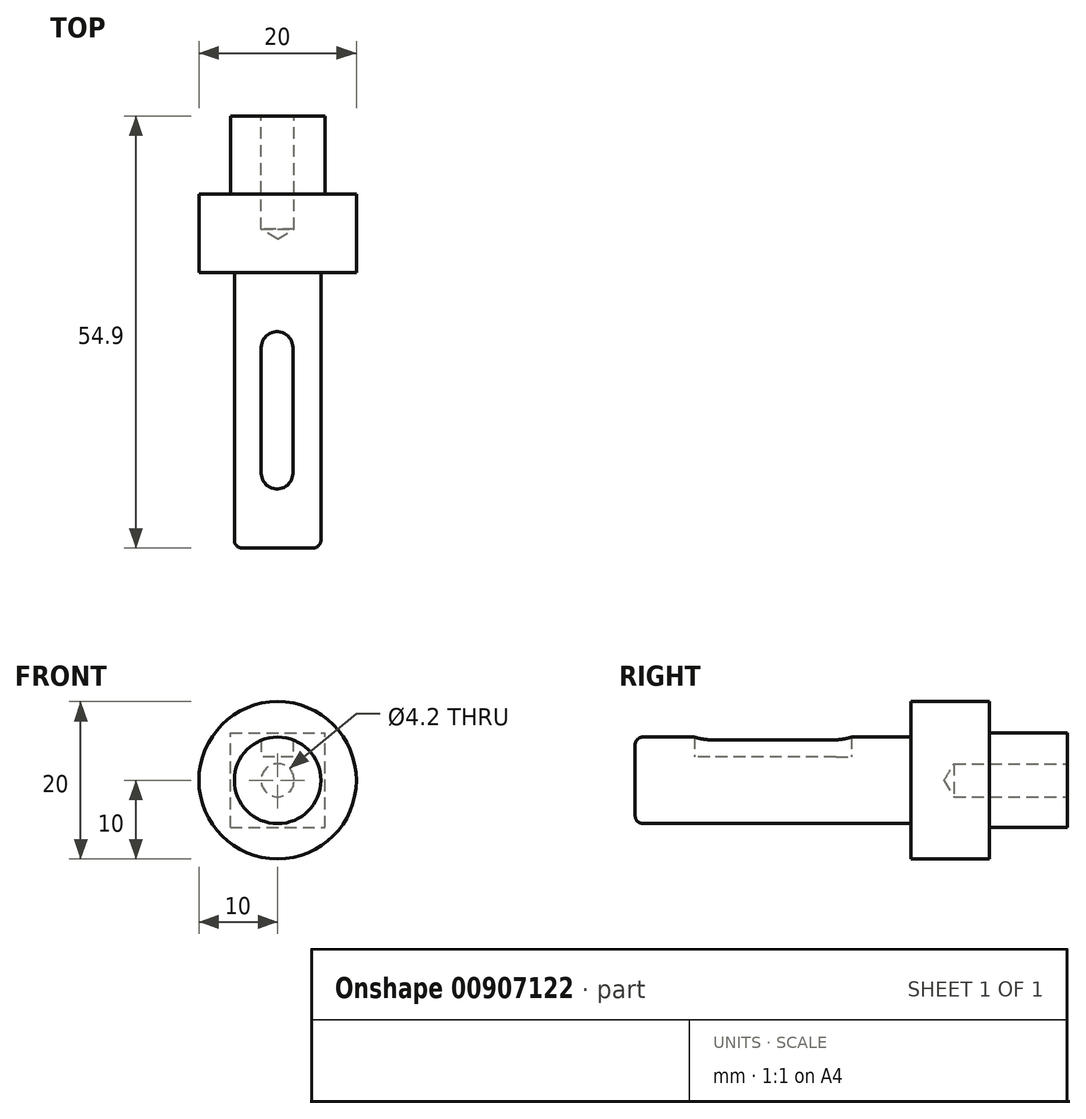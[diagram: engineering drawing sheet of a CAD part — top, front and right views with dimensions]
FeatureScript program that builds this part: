
annotation { "Feature Type Name" : "Feature", "Feature Type Description" : "" }
export const myFeature = defineFeature(function(context is Context, id is Id, definition is map)
    precondition{}
    {
        {
            var Q0;
            Q0=qCreatedBy(makeId("Front.planeOp"),FACE);
            var sketch = newSketch(context, id + "F0", { "sketchPlane" : qUnion([Q0])});
            skCircle(sketch, "E0", {"center": v(0, 0) * mm, "radius": 5.5 * mm});
            skSolve(sketch);
        }
        {
            var Q0;
            Q0 = qSketchRegion(id + "F0", true);
            extrude(context, id + "F1", {"entities" : qUnion([Q0]), "depth" : 35 * mm, "offsetDistance" : 25 * mm});
        }
        {
            var Q0;
            Q0=qCreatedBy(makeId("Front.planeOp"),FACE);
            var sketch = newSketch(context, id + "F2", { "sketchPlane" : qUnion([Q0])});
            skCircle(sketch, "E1", {"center": v(0, 0) * mm, "radius": 10 * mm});
            skSolve(sketch);
        }
        {
            var Q0;
            Q0 = qSketchRegion(id + "F2", true);
            extrude(context, id + "F3", {"entities" : qUnion([Q0]), "operationType" : NewBodyOperationType.ADD, "oppositeDirection" : true, "depth" : 10 * mm, "offsetDistance" : 25 * mm});
        }
        {
            var Q0;
            Q0=makeQuery(id+"F3.opExtrude","CAP_FACE",FACE,{"disambiguationData":[OSD([sQuery(id+"F2.wireOp",EDGE,"E1")])],"isStart":false});
            var sketch = newSketch(context, id + "F4", { "sketchPlane" : qUnion([Q0])});
            skLineSegment(sketch, "E2.bottom", {"start": v(6, -6) * mm, "end": v(-6, -6) * mm});
            skLineSegment(sketch, "E2.top", {"start": v(6, 6) * mm, "end": v(-6, 6) * mm});
            skLineSegment(sketch, "E2.left", {"start": v(6, -6) * mm, "end": v(6, 6) * mm});
            skLineSegment(sketch, "E2.right", {"start": v(-6, -6) * mm, "end": v(-6, 6) * mm});
            skPoint(sketch, "E2.middle", {"position": v(0, 0) * mm});
            skSolve(sketch);
        }
        {
            var Q0;
            Q0 = qSketchRegion(id + "F4", true);
            extrude(context, id + "F5", {"entities" : qUnion([Q0]), "operationType" : NewBodyOperationType.ADD, "depth" : 9.9 * mm, "offsetDistance" : 25 * mm});
        }
        {
            var Q0;
            Q0=makeQuery(id+"F5.opExtrude","CAP_FACE",FACE,{"disambiguationData":[OSD([sQuery(id+"F4.wireOp",EDGE,"E2.bottom"),sQuery(id+"F4.wireOp",EDGE,"E2.top"),sQuery(id+"F4.wireOp",EDGE,"E2.left"),sQuery(id+"F4.wireOp",EDGE,"E2.right")])],"isStart":false});
            var sketch = newSketch(context, id + "F6", { "sketchPlane" : qUnion([Q0])});
            skCircle(sketch, "E3", {"center": v(0, 0) * mm, "radius": 3.38 * mm});
            skSolve(sketch);
        }
        {
            var Q0;
            Q0=sQuery(id+"F6.wireOp",VERTEX,"E3.center");
            var Q1;
            Q1=makeQuery(id+"F1.opExtrude","SWEPT_BODY",BODY,{"disambiguationData":[OSD([sQuery(id+"F0.wireOp",EDGE,"E0")])]});
            hole(context, id + "F7", {"style" : HoleStyle.SIMPLE, "endStyle" : HoleEndStyle.BLIND, "standardTappedOrClearance" : lookupTablePath({ "standard" : "ISO", "engagement" : "75%", "pitch" : "0.8 mm", "size" : "M5", "type" : "Tapped" }), "standardBlindInLast" : lookupTablePath({ "standard" : "ISO", "engagement" : "75%", "pitch" : "0.8 mm", "size" : "M5", "type" : "Tapped" }), "holeDiameter" : 4.2 * mm, "majorDiameter" : 5 * mm, "showTappedDepth" : true, "holeDepth" : 14.4 * mm, "isTappedThrough" : true, "tappedDepth" : 12 * mm, "tapClearance" : 3, "locations" : qUnion([Q0]), "scope" : qUnion([Q1])});
        }
        {
            var Q0;
            Q0=qCreatedBy(makeId("Top.planeOp"),FACE);
            cPlane(context, id + "F8", {"entities" : qUnion([Q0]), "cplaneType" : CPlaneType.OFFSET, "offset" : 3 * mm, "width" : 150 * mm, "height" : 150 * mm});
        }
        {
            var Q0;
            Q0=qCreatedBy(id+"F8.planeOp",FACE);
            var sketch = newSketch(context, id + "F9", { "sketchPlane" : qUnion([Q0])});
            skLineSegment(sketch, "E4", {"start": v(-2.07, -9.5) * mm, "end": v(-2.07, -25.5) * mm});
            skLineSegment(sketch, "E5", {"start": v(1.93, -9.5) * mm, "end": v(1.93, -25.5) * mm});
            skArc(sketch, "E6", {"start": v(1.93, -9.5) * mm, "mid": v(-0.07, -7.5) * mm, "end": v(-2.07, -9.5) * mm});
            skArc(sketch, "E7", {"start": v(-2.07, -25.5) * mm, "mid": v(-0.07, -27.5) * mm, "end": v(1.93, -25.5) * mm});
            skSolve(sketch);
        }
        {
            var Q0;
            Q0 = qSketchRegion(id + "F9", true);
            extrude(context, id + "F10", {"entities" : qUnion([Q0]), "operationType" : NewBodyOperationType.REMOVE, "depth" : 25 * mm, "offsetDistance" : 25 * mm});
        }
        {
            var Q0;
            Q0=makeQuery(id+"F1.opExtrude","CAP_EDGE",EDGE,{"disambiguationData":[OSD([sQuery(id+"F0.wireOp",EDGE,"E0")])],"isStart":false});
            fillet(context, id + "F11", {"entities" : qUnion([Q0]), "radius" : 1 * mm, "tangentPropagation" : true, "allowEdgeOverflow" : false});
        }
    });
